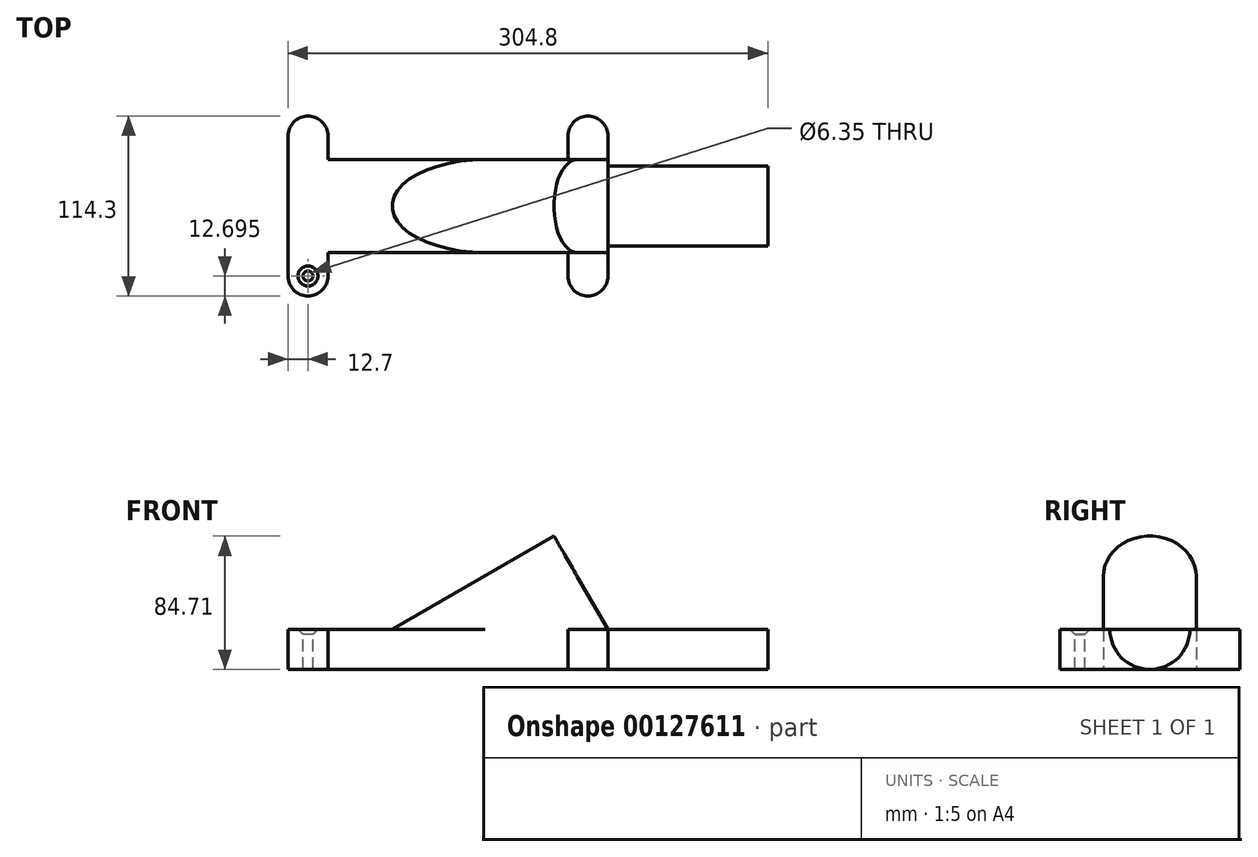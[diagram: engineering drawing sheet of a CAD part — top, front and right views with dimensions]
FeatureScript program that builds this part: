
annotation { "Feature Type Name" : "Feature", "Feature Type Description" : "" }
export const myFeature = defineFeature(function(context is Context, id is Id, definition is map)
    precondition{}
    {
        {
            var Q0;
            Q0=qCreatedBy(makeId("Top.planeOp"),FACE);
            var sketch = newSketch(context, id + "F0", { "sketchPlane" : qUnion([Q0])});
            skLineSegment(sketch, "E0", {"start": v(0, 0) * mm, "end": v(76.2, 0) * mm});
            skLineSegment(sketch, "E1", {"start": v(76.2, 0) * mm, "end": v(76.2, 14.94) * mm});
            skLineSegment(sketch, "E2", {"start": v(101.6, 14.94) * mm, "end": v(101.6, -73.96) * mm});
            skLineSegment(sketch, "E3", {"start": v(0, -59.03) * mm, "end": v(0, 0) * mm});
            skLineSegment(sketch, "E4", {"start": v(0, -59.03) * mm, "end": v(76.2, -59.03) * mm});
            skLineSegment(sketch, "E5", {"start": v(76.2, -59.03) * mm, "end": v(76.2, -73.96) * mm});
            skPoint(sketch, "E6.MirrorCS.end.orphan", {"position": v(-76.2, 0) * mm});
            skPoint(sketch, "E6.MirrorCS.start.orphan", {"position": v(0, 0) * mm});
            skPoint(sketch, "E7.MirrorCS.end.orphan", {"position": v(-76.2, 14.94) * mm});
            skPoint(sketch, "E8.orphan", {"position": v(0, -73.96) * mm});
            skLineSegment(sketch, "E9.MirrorCS", {"start": v(-76.2, 0) * mm, "end": v(-76.2, 14.94) * mm});
            skLineSegment(sketch, "E10.MirrorCS", {"start": v(0, -59.03) * mm, "end": v(-76.2, -59.03) * mm});
            skLineSegment(sketch, "E11.MirrorCS", {"start": v(0, 0) * mm, "end": v(-76.2, 0) * mm});
            skLineSegment(sketch, "E12.MirrorCS", {"start": v(-101.6, 14.94) * mm, "end": v(-101.6, -73.96) * mm});
            skLineSegment(sketch, "E13.MirrorCS", {"start": v(-76.2, -59.03) * mm, "end": v(-76.2, -73.96) * mm});
            skArc(sketch, "E14", {"start": v(-76.2, 14.94) * mm, "mid": v(-88.9, 27.64) * mm, "end": v(-101.6, 14.94) * mm});
            skArc(sketch, "E15", {"start": v(101.6, 14.94) * mm, "mid": v(88.9, 27.64) * mm, "end": v(76.2, 14.94) * mm});
            skArc(sketch, "E16", {"start": v(76.2, -73.96) * mm, "mid": v(88.9, -86.66) * mm, "end": v(101.6, -73.96) * mm});
            skArc(sketch, "E17", {"start": v(-101.6, -73.96) * mm, "mid": v(-88.9, -86.66) * mm, "end": v(-76.2, -73.96) * mm});
            skSolve(sketch);
        }
        {
            var Q0;
            Q0=makeQuery(id+"F0.imprint","IMPRINT",FACE,{"disambiguationData":[TD([[makeQuery(id+"F0.imprint","IMPRINT",EDGE,{"derivedFrom":sQuery(id+"F0.wireOp",EDGE,"E3")}),1.0]])]});
            var Q1;
            Q1=makeQuery(id+"F0.imprint","IMPRINT",FACE,{"disambiguationData":[TD([[makeQuery(id+"F0.imprint","IMPRINT",EDGE,{"derivedFrom":sQuery(id+"F0.wireOp",EDGE,"E0")}),-1.0]])]});
            extrude(context, id + "F1", {"entities" : qUnion([Q0, Q1]), "depth" : 25.4 * mm});
        }
        {
            var Q0;
            Q0=makeQuery(id+"F1.opExtrude","CAP_EDGE",EDGE,{"disambiguationData":[OSD([sQuery(id+"F0.wireOp",EDGE,"E2")])],"isStart":false});
            var Q1;
            Q1=makeQuery(id+"F1.opExtrude","CAP_FACE",FACE,{"disambiguationData":[OSD([sQuery(id+"F0.wireOp",EDGE,"E0"),sQuery(id+"F0.wireOp",EDGE,"E1"),sQuery(id+"F0.wireOp",EDGE,"E2"),sQuery(id+"F0.wireOp",EDGE,"E4"),sQuery(id+"F0.wireOp",EDGE,"E5"),sQuery(id+"F0.wireOp",EDGE,"E9.MirrorCS"),sQuery(id+"F0.wireOp",EDGE,"E10.MirrorCS"),sQuery(id+"F0.wireOp",EDGE,"E11.MirrorCS"),sQuery(id+"F0.wireOp",EDGE,"E12.MirrorCS"),sQuery(id+"F0.wireOp",EDGE,"E13.MirrorCS"),sQuery(id+"F0.wireOp",EDGE,"E14"),sQuery(id+"F0.wireOp",EDGE,"E15"),sQuery(id+"F0.wireOp",EDGE,"E16"),sQuery(id+"F0.wireOp",EDGE,"E17")])],"isStart":false});
            cPlane(context, id + "F2", {"entities" : qUnion([Q0, Q1]), "cplaneType" : CPlaneType.LINE_ANGLE, "offset" : 25.4 * mm, "angle" : 120 * degree, "width" : 152.4 * mm, "height" : 152.4 * mm});
        }
        {
            var Q0;
            Q0=qCreatedBy(id+"F2.planeOp",FACE);
            var sketch = newSketch(context, id + "F3", { "sketchPlane" : qUnion([Q0])});
            skLineSegment(sketch, "E18", {"start": v(-59.03, -28.8) * mm, "end": v(-59.03, 10.16) * mm});
            skArc(sketch, "E19", {"start": v(0, 10.16) * mm, "mid": v(-29.51, 39.68) * mm, "end": v(-59.03, 10.16) * mm});
            skLineSegment(sketch, "E20", {"start": v(0, 10.16) * mm, "end": v(0, -28.8) * mm});
            skLineSegment(sketch, "E21", {"start": v(0, -28.8) * mm, "end": v(-59.03, -28.8) * mm});
            skSolve(sketch);
        }
        {
            var Q0;
            Q0=makeQuery(id+"F3.imprint","IMPRINT",FACE,{"disambiguationData":[TD([[makeQuery(id+"F3.imprint","IMPRINT",EDGE,{"derivedFrom":sQuery(id+"F3.wireOp",EDGE,"E18")}),-1.0]])]});
            extrude(context, id + "F4", {"entities" : qUnion([Q0]), "operationType" : NewBodyOperationType.ADD, "endBound" : BoundingType.UP_TO_NEXT, "oppositeDirection" : true, "depth" : 42.83 * mm});
        }
        {
            var Q0;
            Q0=makeQuery(id+"F1.opExtrude","SWEPT_FACE",FACE,{"disambiguationData":[OSD([sQuery(id+"F0.wireOp",EDGE,"E2")])]});
            var sketch = newSketch(context, id + "F5", { "sketchPlane" : qUnion([Q0])});
            skCircle(sketch, "E22", {"center": v(-29.51, 25.4) * mm, "radius": 25.4 * mm});
            skSolve(sketch);
        }
        {
            var Q0;
            {var subQ0=sQuery(id+"F5.wireOp",EDGE,"E22");var subQ1=sQuery(id+"F0.wireOp",EDGE,"E2");var subQ2=makeQuery(id+"F4.boolean.opBoolean","MERGE",EDGE,{"derivedFrom":[makeQuery(id+"F1.opExtrude","CAP_EDGE",EDGE,{"disambiguationData":[OSD([subQ1])],"isStart":false}),makeQuery(id+"F4.opExtrude","TWEAK_EDGE",EDGE,{"derivedFrom":[makeQuery(id+"F1.opExtrude","CAP_FACE",FACE,{"disambiguationData":[OSD([sQuery(id+"F0.wireOp",EDGE,"E0"),sQuery(id+"F0.wireOp",EDGE,"E1"),subQ1,sQuery(id+"F0.wireOp",EDGE,"E4"),sQuery(id+"F0.wireOp",EDGE,"E5"),sQuery(id+"F0.wireOp",EDGE,"E9.MirrorCS"),sQuery(id+"F0.wireOp",EDGE,"E10.MirrorCS"),sQuery(id+"F0.wireOp",EDGE,"E11.MirrorCS"),sQuery(id+"F0.wireOp",EDGE,"E12.MirrorCS"),sQuery(id+"F0.wireOp",EDGE,"E13.MirrorCS"),sQuery(id+"F0.wireOp",EDGE,"E14"),sQuery(id+"F0.wireOp",EDGE,"E15"),sQuery(id+"F0.wireOp",EDGE,"E16"),sQuery(id+"F0.wireOp",EDGE,"E17")])],"isStart":false}),makeQuery(id+"F3.imprint","IMPRINT",EDGE,{"derivedFrom":sQuery(id+"F3.wireOp",EDGE,"E18")}),makeQuery(id+"F3.imprint","IMPRINT",EDGE,{"derivedFrom":sQuery(id+"F3.wireOp",EDGE,"E19")}),makeQuery(id+"F3.imprint","IMPRINT",EDGE,{"derivedFrom":sQuery(id+"F3.wireOp",EDGE,"E20")}),makeQuery(id+"F3.imprint","IMPRINT",EDGE,{"derivedFrom":sQuery(id+"F3.wireOp",EDGE,"E21")})]})]});var subQ3=makeQuery(id+"F5.imprint","INTERSECT",VERTEX,{"disambiguationData":[OD(0.0)],"derivedFrom":[subQ2,subQ0]});Q0=makeQuery(id+"F5.imprint","IMPRINT",FACE,{"disambiguationData":[TD([[makeQuery(id+"F5.imprint","IMPRINT",EDGE,{"disambiguationData":[TD([[subQ3,1.0]])],"derivedFrom":subQ0}),1.0]])]});}
            var Q1;
            {var subQ0=sQuery(id+"F5.wireOp",EDGE,"E22");var subQ1=sQuery(id+"F0.wireOp",EDGE,"E2");var subQ4=makeQuery(id+"F5.imprint","INTERSECT",VERTEX,{"derivedFrom":[makeQuery(id+"F1.opExtrude","CAP_EDGE",EDGE,{"disambiguationData":[OSD([subQ1])],"isStart":true}),subQ0]});Q1=makeQuery(id+"F5.imprint","IMPRINT",FACE,{"disambiguationData":[TD([[makeQuery(id+"F5.imprint","IMPRINT",EDGE,{"disambiguationData":[TD([[subQ4,1.0]])],"derivedFrom":subQ0}),1.0]])]});}
            extrude(context, id + "F6", {"entities" : qUnion([Q0, Q1]), "operationType" : NewBodyOperationType.ADD, "depth" : 101.6 * mm});
        }
        {
            var Q0;
            Q0=makeQuery(id+"F6.opExtrude","CAP_FACE",FACE,{"disambiguationData":[OSD([sQuery(id+"F5.wireOp",EDGE,"E22")])],"isStart":false});
            var sketch = newSketch(context, id + "F7", { "sketchPlane" : qUnion([Q0])});
            skLineSegment(sketch, "E23", {"start": v(-54.91, 25.4) * mm, "end": v(-4.11, 25.4) * mm});
            skSolve(sketch);
        }
        {
            var Q0;
            Q0=sQuery(id+"F7.wireOp",EDGE,"E23");
            var Q1;
            Q1=makeQuery(id+"F6.opExtrude","SWEPT_FACE",FACE,{"disambiguationData":[OSD([sQuery(id+"F5.wireOp",EDGE,"E22")])]});
            cPlane(context, id + "F8", {"entities" : qUnion([Q0, Q1]), "cplaneType" : CPlaneType.LINE_ANGLE, "offset" : 25.4 * mm, "angle" : 45 * degree, "width" : 152.4 * mm, "height" : 152.4 * mm});
        }
        {
            var Q0;
            {var subQ0=sQuery(id+"F0.wireOp",EDGE,"E9.MirrorCS");var subQ1=sQuery(id+"F0.wireOp",EDGE,"E10.MirrorCS");var subQ2=sQuery(id+"F0.wireOp",EDGE,"E4");var subQ3=sQuery(id+"F0.wireOp",EDGE,"E12.MirrorCS");var subQ4=sQuery(id+"F0.wireOp",EDGE,"E11.MirrorCS");var subQ5=sQuery(id+"F0.wireOp",EDGE,"E0");var subQ6=sQuery(id+"F0.wireOp",EDGE,"E17");var subQ7=sQuery(id+"F0.wireOp",EDGE,"E13.MirrorCS");var subQ8=sQuery(id+"F0.wireOp",EDGE,"E14");Q0=makeQuery(id+"F4.boolean.opBoolean","SPLIT",FACE,{"disambiguationData":[TD([makeQuery(id+"F1.opExtrude","SWEPT_FACE",FACE,{"disambiguationData":[OSD([subQ0])]})])],"derivedFrom":makeQuery(id+"F1.opExtrude","CAP_FACE",FACE,{"disambiguationData":[OSD([subQ5,sQuery(id+"F0.wireOp",EDGE,"E1"),sQuery(id+"F0.wireOp",EDGE,"E2"),subQ2,sQuery(id+"F0.wireOp",EDGE,"E5"),subQ0,subQ1,subQ4,subQ3,subQ7,subQ8,sQuery(id+"F0.wireOp",EDGE,"E15"),sQuery(id+"F0.wireOp",EDGE,"E16"),subQ6])],"isStart":false})});}
            var sketch = newSketch(context, id + "F9", { "sketchPlane" : qUnion([Q0])});
            skCircle(sketch, "E24", {"center": v(-88.9, -73.96) * mm, "radius": 6.35 * mm});
            skSolve(sketch);
        }
        {
            var Q0;
            Q0=sQuery(id+"F9.wireOp",VERTEX,"E24.center");
            var Q1;
            Q1=makeQuery(id+"F1.opExtrude","SWEPT_BODY",BODY,{"disambiguationData":[OSD([sQuery(id+"F0.wireOp",EDGE,"E0"),sQuery(id+"F0.wireOp",EDGE,"E1"),sQuery(id+"F0.wireOp",EDGE,"E2"),sQuery(id+"F0.wireOp",EDGE,"E4"),sQuery(id+"F0.wireOp",EDGE,"E5"),sQuery(id+"F0.wireOp",EDGE,"E9.MirrorCS"),sQuery(id+"F0.wireOp",EDGE,"E10.MirrorCS"),sQuery(id+"F0.wireOp",EDGE,"E11.MirrorCS"),sQuery(id+"F0.wireOp",EDGE,"E12.MirrorCS"),sQuery(id+"F0.wireOp",EDGE,"E13.MirrorCS"),sQuery(id+"F0.wireOp",EDGE,"E14"),sQuery(id+"F0.wireOp",EDGE,"E15"),sQuery(id+"F0.wireOp",EDGE,"E16"),sQuery(id+"F0.wireOp",EDGE,"E17")])]});
            hole(context, id + "F10", {"style" : HoleStyle.C_SINK, "endStyle" : HoleEndStyle.THROUGH, "holeDiameter" : 6.35 * mm, "cSinkDiameter" : 12.7 * mm, "cSinkAngle" : 90 * degree, "locations" : qUnion([Q0]), "scope" : qUnion([Q1]), "isTappedThrough" : true});
        }
    });
